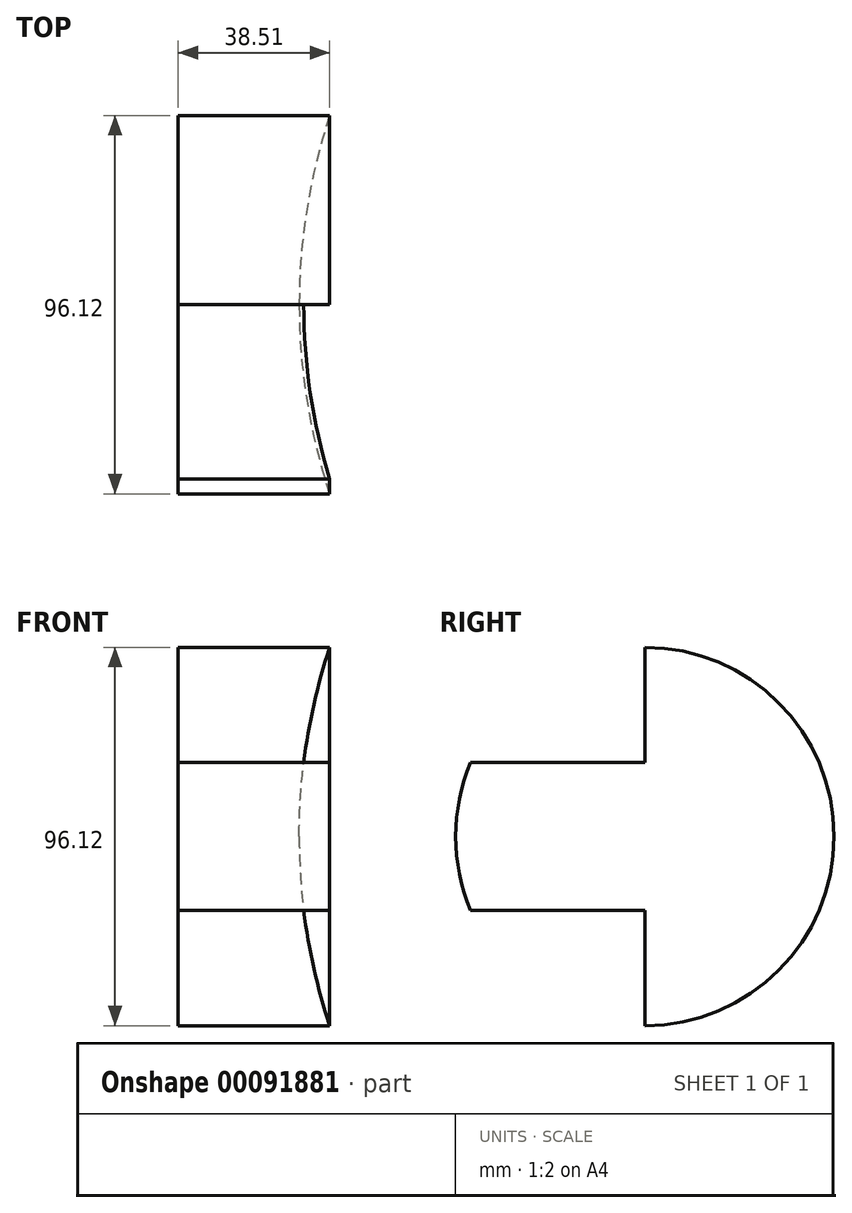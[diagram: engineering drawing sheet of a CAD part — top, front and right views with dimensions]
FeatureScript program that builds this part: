
annotation { "Feature Type Name" : "Feature", "Feature Type Description" : "" }
export const myFeature = defineFeature(function(context is Context, id is Id, definition is map)
    precondition{}
    {
        {
            var Q0;
            Q0=qCreatedBy(makeId("Front.planeOp"),FACE);
            var sketch = newSketch(context, id + "F0", { "sketchPlane" : qUnion([Q0])});
            skLineSegment(sketch, "E0.bottom", {"start": v(0, 0) * mm, "end": v(-38.51, 0) * mm});
            skLineSegment(sketch, "E0.top", {"start": v(0, 48.06) * mm, "end": v(-38.51, 48.06) * mm});
            skLineSegment(sketch, "E0.right", {"start": v(-38.51, 0) * mm, "end": v(-38.51, 48.06) * mm});
            skArc(sketch, "E1", {"start": v(0, 48.06) * mm, "mid": v(-5.81, 24.34) * mm, "end": v(-7.77, 0) * mm});
            skSolve(sketch);
        }
        {
            var Q0;
            Q0=makeQuery(id+"F0.imprint","IMPRINT",FACE,{"disambiguationData":[TD([[makeQuery(id+"F0.imprint","IMPRINT",EDGE,{"derivedFrom":sQuery(id+"F0.wireOp",EDGE,"E0.top")}),1.0]])]});
            var Q1;
            Q1=sQuery(id+"F0.wireOp",EDGE,"E0.bottom");
            revolve(context, id + "F1", {"entities" : qUnion([Q0]), "axis" : qUnion([Q1]), "revolveType" : RevolveType.FULL});
        }
        {
            var Q0;
            Q0=qCreatedBy(makeId("Right.planeOp"),FACE);
            var sketch = newSketch(context, id + "F2", { "sketchPlane" : qUnion([Q0])});
            skLineSegment(sketch, "E2.bottom", {"start": v(0, 18.79) * mm, "end": v(-39.77, 18.79) * mm});
            skLineSegment(sketch, "E2.top", {"start": v(0, -18.79) * mm, "end": v(-39.77, -18.79) * mm});
            skLineSegment(sketch, "E2.left", {"start": v(0, 18.79) * mm, "end": v(0, -18.79) * mm});
            skLineSegment(sketch, "E2.right", {"start": v(-39.77, 18.79) * mm, "end": v(-39.77, -18.79) * mm});
            skPoint(sketch, "E2.middle", {"position": v(-19.88, 0) * mm});
            skLineSegment(sketch, "E3.bottom", {"start": v(0, -18.79) * mm, "end": v(-63.72, -18.79) * mm});
            skLineSegment(sketch, "E3.top", {"start": v(0, -68.26) * mm, "end": v(-63.72, -68.26) * mm});
            skLineSegment(sketch, "E3.left", {"start": v(0, -18.79) * mm, "end": v(0, -68.26) * mm});
            skLineSegment(sketch, "E3.right", {"start": v(-63.72, -18.79) * mm, "end": v(-63.72, -68.26) * mm});
            skLineSegment(sketch, "E4.bottom", {"start": v(0, 18.79) * mm, "end": v(-63.72, 18.79) * mm});
            skLineSegment(sketch, "E4.top", {"start": v(0, 53.23) * mm, "end": v(-63.72, 53.23) * mm});
            skLineSegment(sketch, "E4.left", {"start": v(0, 18.79) * mm, "end": v(0, 53.23) * mm});
            skLineSegment(sketch, "E4.right", {"start": v(-63.72, 18.79) * mm, "end": v(-63.72, 53.23) * mm});
            skLineSegment(sketch, "E5.bottom", {"start": v(-63.72, -18.79) * mm, "end": v(-39.77, -18.79) * mm});
            skLineSegment(sketch, "E5.top", {"start": v(-63.72, 18.79) * mm, "end": v(-39.77, 18.79) * mm});
            skLineSegment(sketch, "E5.left", {"start": v(-63.72, -18.79) * mm, "end": v(-63.72, 18.79) * mm});
            skLineSegment(sketch, "E5.right", {"start": v(-39.77, -18.79) * mm, "end": v(-39.77, 18.79) * mm});
            skSolve(sketch);
        }
        {
            var Q0;
            Q0=makeQuery(id+"F2.imprint","IMPRINT",FACE,{"disambiguationData":[TD([[makeQuery(id+"F2.imprint","IMPRINT",EDGE,{"derivedFrom":sQuery(id+"F2.wireOp",EDGE,"E3.bottom")}),1.0]])]});
            var Q1;
            Q1=makeQuery(id+"F2.imprint","IMPRINT",FACE,{"disambiguationData":[TD([[makeQuery(id+"F2.imprint","IMPRINT",EDGE,{"derivedFrom":sQuery(id+"F2.wireOp",EDGE,"E5.bottom")}),1.0]])]});
            var Q2;
            Q2=makeQuery(id+"F2.imprint","IMPRINT",FACE,{"disambiguationData":[TD([[makeQuery(id+"F2.imprint","IMPRINT",EDGE,{"derivedFrom":sQuery(id+"F2.wireOp",EDGE,"E4.bottom")}),-1.0]])]});
            extrude(context, id + "F3", {"entities" : qUnion([Q0, Q1, Q2]), "operationType" : NewBodyOperationType.REMOVE, "depth" : 123 * mm, "symmetric" : true});
        }
    });
